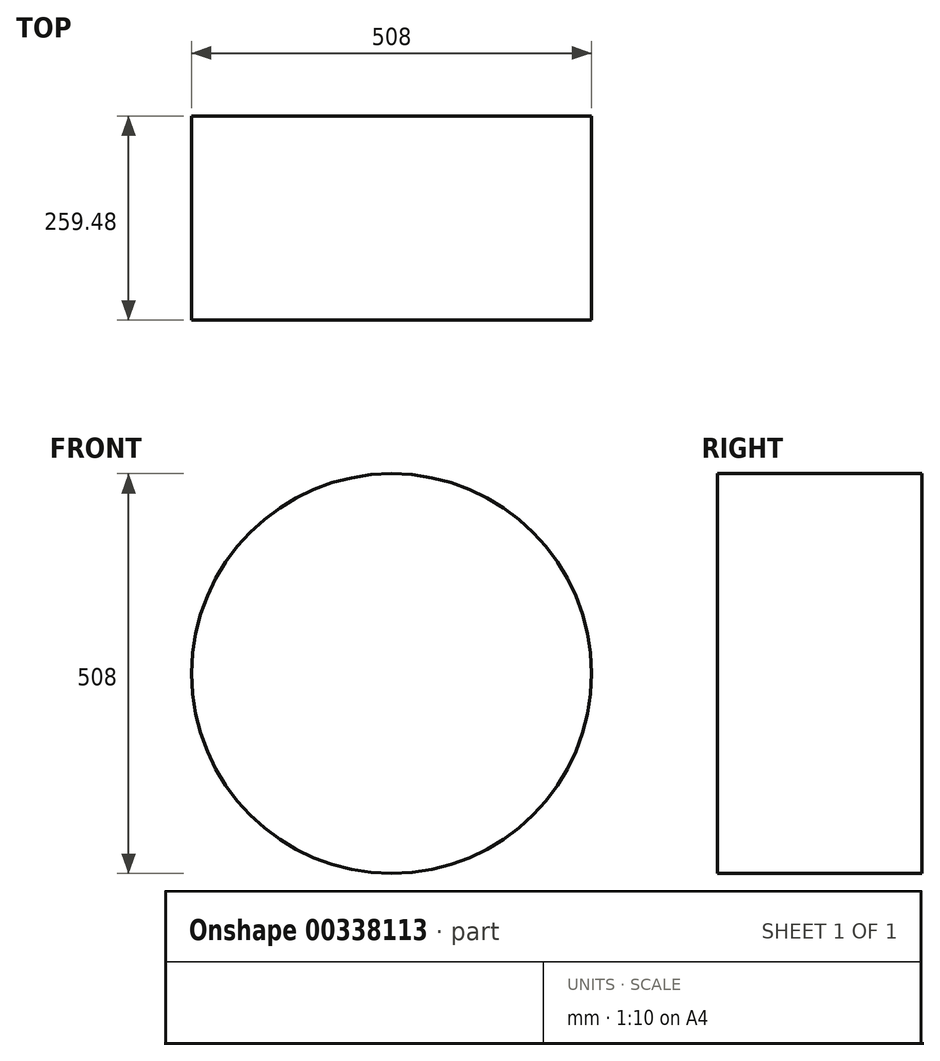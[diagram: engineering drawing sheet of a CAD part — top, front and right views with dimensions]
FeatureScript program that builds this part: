
annotation { "Feature Type Name" : "Feature", "Feature Type Description" : "" }
export const myFeature = defineFeature(function(context is Context, id is Id, definition is map)
    precondition{}
    {
        {
            var Q0;
            Q0=qCreatedBy(makeId("Front.planeOp"),FACE);
            var sketch = newSketch(context, id + "F0", { "sketchPlane" : qUnion([Q0])});
            skCircle(sketch, "E0", {"center": v(0, 0) * mm, "radius": 254 * mm});
            skSolve(sketch);
        }
        {
            var Q0;
            Q0=makeQuery(id+"F0.imprint","IMPRINT",FACE,{"disambiguationData":[TD([[makeQuery(id+"F0.imprint","IMPRINT",EDGE,{"derivedFrom":sQuery(id+"F0.wireOp",EDGE,"E0")}),1.0]])]});
            extrude(context, id + "F1", {"entities" : qUnion([Q0]), "depth" : 259.48 * mm});
        }
    });
